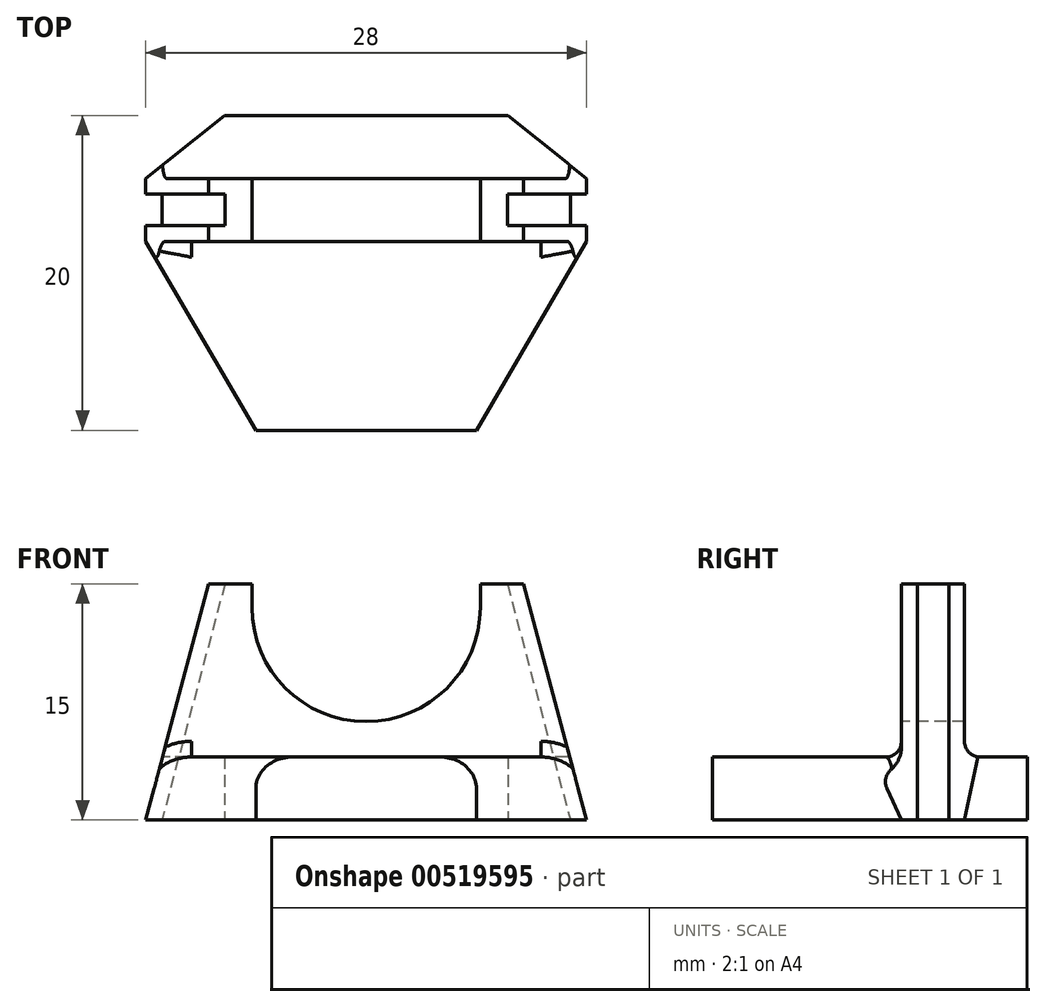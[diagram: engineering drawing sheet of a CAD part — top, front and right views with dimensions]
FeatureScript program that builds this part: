
annotation { "Feature Type Name" : "Feature", "Feature Type Description" : "" }
export const myFeature = defineFeature(function(context is Context, id is Id, definition is map)
    precondition{}
    {
        {
            var Q0;
            Q0=qCreatedBy(makeId("Top.planeOp"),FACE);
            var sketch = newSketch(context, id + "F0", { "sketchPlane" : qUnion([Q0])});
            skLineSegment(sketch, "E0.bottom", {"start": v(-14, 10) * mm, "end": v(14, 10) * mm});
            skLineSegment(sketch, "E0.top", {"start": v(-14, -10) * mm, "end": v(14, -10) * mm});
            skLineSegment(sketch, "E0.left", {"start": v(-14, 10) * mm, "end": v(-14, -10) * mm});
            skLineSegment(sketch, "E0.right", {"start": v(14, 10) * mm, "end": v(14, -10) * mm});
            skSolve(sketch);
        }
        {
            var Q0;
            Q0 = qSketchRegion(id + "F0", true);
            extrude(context, id + "F1", {"entities" : qUnion([Q0]), "depth" : 15 * mm, "offsetDistance" : 25 * mm});
        }
        {
            var Q0;
            Q0=qCreatedBy(makeId("Right.planeOp"),FACE);
            var sketch = newSketch(context, id + "F2", { "sketchPlane" : qUnion([Q0])});
            skLineSegment(sketch, "E1.bottom", {"start": v(-10, 15) * mm, "end": v(2, 15) * mm});
            skLineSegment(sketch, "E1.top", {"start": v(-10, 4) * mm, "end": v(2, 4) * mm});
            skLineSegment(sketch, "E1.left", {"start": v(-10, 15) * mm, "end": v(-10, 4) * mm});
            skLineSegment(sketch, "E1.right", {"start": v(2, 15) * mm, "end": v(2, 4) * mm});
            skSolve(sketch);
        }
        {
            var Q0;
            Q0 = qSketchRegion(id + "F2", true);
            extrude(context, id + "F3", {"entities" : qUnion([Q0]), "endBound" : BoundingType.SYMMETRIC, "depth" : 28 * mm, "offsetDistance" : 25 * mm});
        }
        {
            var Q0;
            Q0=qCreatedBy(makeId("Front.planeOp"),FACE);
            var sketch = newSketch(context, id + "F4", { "sketchPlane" : qUnion([Q0])});
            skCircle(sketch, "E2", {"center": v(0, 13.5) * mm, "radius": 7.25 * mm});
            skLineSegment(sketch, "E3.bottom", {"start": v(-7.25, 13.5) * mm, "end": v(7.25, 13.5) * mm});
            skLineSegment(sketch, "E3.top", {"start": v(-7.25, 22.5) * mm, "end": v(7.25, 22.5) * mm});
            skLineSegment(sketch, "E3.left", {"start": v(-7.25, 13.5) * mm, "end": v(-7.25, 22.5) * mm});
            skLineSegment(sketch, "E3.right", {"start": v(7.25, 13.5) * mm, "end": v(7.25, 22.5) * mm});
            skSolve(sketch);
        }
        {
            var Q0;
            Q0 = qSketchRegion(id + "F4", true);
            extrude(context, id + "F5", {"entities" : qUnion([Q0]), "oppositeDirection" : true, "depth" : 25 * mm, "offsetDistance" : 25 * mm});
        }
        {
            var Q0;
            Q0=qCreatedBy(makeId("Front.planeOp"),FACE);
            var sketch = newSketch(context, id + "F6", { "sketchPlane" : qUnion([Q0])});
            skLineSegment(sketch, "E4", {"start": v(-14, 15) * mm, "end": v(-10, 15) * mm});
            skLineSegment(sketch, "E5", {"start": v(-10, 15) * mm, "end": v(-14, 0) * mm});
            skLineSegment(sketch, "E6", {"start": v(-14, 0) * mm, "end": v(-14, 15) * mm});
            skSolve(sketch);
        }
        {
            var Q0;
            Q0 = qSketchRegion(id + "F6", true);
            extrude(context, id + "F7", {"entities" : qUnion([Q0]), "endBound" : BoundingType.SYMMETRIC, "depth" : 20 * mm, "offsetDistance" : 25 * mm});
        }
        {
            var Q0;
            Q0=makeQuery(id+"F7.opExtrude","SWEPT_BODY",BODY,{"disambiguationData":[OSD([sQuery(id+"F6.wireOp",EDGE,"E4"),sQuery(id+"F6.wireOp",EDGE,"E5"),sQuery(id+"F6.wireOp",EDGE,"E6")])]});
            var Q1;
            Q1=qCreatedBy(makeId("Right.planeOp"),FACE);
            mirror(context, id + "F8", {"entities" : qUnion([Q0]), "mirrorPlane" : qUnion([Q1])});
        }
        {
            var Q0;
            Q0=qCreatedBy(makeId("Right.planeOp"),FACE);
            var sketch = newSketch(context, id + "F9", { "sketchPlane" : qUnion([Q0])});
            skLineSegment(sketch, "E7.bottom", {"start": v(6, 15) * mm, "end": v(10, 15) * mm});
            skLineSegment(sketch, "E7.top", {"start": v(6, 4) * mm, "end": v(10, 4) * mm});
            skLineSegment(sketch, "E7.left", {"start": v(6, 15) * mm, "end": v(6, 4) * mm});
            skLineSegment(sketch, "E7.right", {"start": v(10, 15) * mm, "end": v(10, 4) * mm});
            skSolve(sketch);
        }
        {
            var Q0;
            Q0 = qSketchRegion(id + "F9", true);
            extrude(context, id + "F10", {"entities" : qUnion([Q0]), "endBound" : BoundingType.SYMMETRIC, "depth" : 28 * mm, "offsetDistance" : 25 * mm});
        }
        {
            var Q0;
            Q0=qCreatedBy(makeId("Top.planeOp"),FACE);
            var sketch = newSketch(context, id + "F11", { "sketchPlane" : qUnion([Q0])});
            skLineSegment(sketch, "E8", {"start": v(-9, 10) * mm, "end": v(-14, 10) * mm});
            skLineSegment(sketch, "E9", {"start": v(-14, 10) * mm, "end": v(-14, 6) * mm});
            skLineSegment(sketch, "E10", {"start": v(-14, 6) * mm, "end": v(-9, 10) * mm});
            skSolve(sketch);
        }
        {
            var Q0;
            Q0 = qSketchRegion(id + "F11", true);
            extrude(context, id + "F12", {"entities" : qUnion([Q0]), "depth" : 15 * mm, "offsetDistance" : 25 * mm});
        }
        {
            var Q0;
            Q0=makeQuery(id+"F12.opExtrude","SWEPT_BODY",BODY,{"disambiguationData":[OSD([sQuery(id+"F11.wireOp",EDGE,"E8"),sQuery(id+"F11.wireOp",EDGE,"E9"),sQuery(id+"F11.wireOp",EDGE,"E10")])]});
            var Q1;
            Q1=qCreatedBy(makeId("Right.planeOp"),FACE);
            mirror(context, id + "F13", {"entities" : qUnion([Q0]), "mirrorPlane" : qUnion([Q1])});
        }
        {
            var Q0;
            Q0=qCreatedBy(makeId("Top.planeOp"),FACE);
            var sketch = newSketch(context, id + "F14", { "sketchPlane" : qUnion([Q0])});
            skLineSegment(sketch, "E11", {"start": v(-7, -10) * mm, "end": v(-14, -10) * mm});
            skLineSegment(sketch, "E12", {"start": v(-14, -10) * mm, "end": v(-14, 2) * mm});
            skLineSegment(sketch, "E13", {"start": v(-14, 2) * mm, "end": v(-7, -10) * mm});
            skSolve(sketch);
        }
        {
            var Q0;
            Q0 = qSketchRegion(id + "F14", true);
            extrude(context, id + "F15", {"entities" : qUnion([Q0]), "depth" : 15 * mm, "offsetDistance" : 25 * mm});
        }
        {
            var Q0;
            Q0=makeQuery(id+"F15.opExtrude","SWEPT_BODY",BODY,{"disambiguationData":[OSD([sQuery(id+"F14.wireOp",EDGE,"E11"),sQuery(id+"F14.wireOp",EDGE,"E12"),sQuery(id+"F14.wireOp",EDGE,"E13")])]});
            var Q1;
            Q1=qCreatedBy(makeId("Right.planeOp"),FACE);
            mirror(context, id + "F16", {"entities" : qUnion([Q0]), "mirrorPlane" : qUnion([Q1])});
        }
        {
            var Q0;
            Q0=makeQuery(id+"F3.opExtrude","SWEPT_BODY",BODY,{"disambiguationData":[OSD([sQuery(id+"F2.wireOp",EDGE,"E1.bottom"),sQuery(id+"F2.wireOp",EDGE,"E1.top"),sQuery(id+"F2.wireOp",EDGE,"E1.left"),sQuery(id+"F2.wireOp",EDGE,"E1.right")])]});
            var Q1;
            Q1=makeQuery(id+"F5.opExtrude","SWEPT_BODY",BODY,{"disambiguationData":[OSD([sQuery(id+"F4.wireOp",EDGE,"E2"),sQuery(id+"F4.wireOp",EDGE,"E3.top"),sQuery(id+"F4.wireOp",EDGE,"E3.left"),sQuery(id+"F4.wireOp",EDGE,"E3.right")])]});
            var Q2;
            Q2=makeQuery(id+"F7.opExtrude","SWEPT_BODY",BODY,{"disambiguationData":[OSD([sQuery(id+"F6.wireOp",EDGE,"E4"),sQuery(id+"F6.wireOp",EDGE,"E5"),sQuery(id+"F6.wireOp",EDGE,"E6")])]});
            var Q3;
            Q3=makeQuery(id+"F8.opPattern","COPY",BODY,{"derivedFrom":makeQuery(id+"F7.opExtrude","SWEPT_BODY",BODY,{"disambiguationData":[OSD([sQuery(id+"F6.wireOp",EDGE,"E4"),sQuery(id+"F6.wireOp",EDGE,"E5"),sQuery(id+"F6.wireOp",EDGE,"E6")])]}),"instanceName":"1"});
            var Q4;
            Q4=makeQuery(id+"F10.opExtrude","SWEPT_BODY",BODY,{"disambiguationData":[OSD([sQuery(id+"F9.wireOp",EDGE,"E7.bottom"),sQuery(id+"F9.wireOp",EDGE,"E7.top"),sQuery(id+"F9.wireOp",EDGE,"E7.left"),sQuery(id+"F9.wireOp",EDGE,"E7.right")])]});
            var Q5;
            Q5=makeQuery(id+"FawOFgsiVvA8u39_4.opExtrude","SWEPT_BODY",BODY,{"disambiguationData":[OSD([sQuery(id+"FQr5FlxrUfjwjdP_4.wireOp",EDGE,"HyzrT1vO-Ye7J-sqqj-sUMt-KC3yQP7SDtpv.bottom"),sQuery(id+"FQr5FlxrUfjwjdP_4.wireOp",EDGE,"HyzrT1vO-Ye7J-sqqj-sUMt-KC3yQP7SDtpv.top"),sQuery(id+"FQr5FlxrUfjwjdP_4.wireOp",EDGE,"HyzrT1vO-Ye7J-sqqj-sUMt-KC3yQP7SDtpv.left"),sQuery(id+"FQr5FlxrUfjwjdP_4.wireOp",EDGE,"HyzrT1vO-Ye7J-sqqj-sUMt-KC3yQP7SDtpv.right")])]});
            var Q6;
            Q6=makeQuery(id+"FKkhov8mjdonEyy_5.opPattern","COPY",BODY,{"derivedFrom":makeQuery(id+"FawOFgsiVvA8u39_4.opExtrude","SWEPT_BODY",BODY,{"disambiguationData":[OSD([sQuery(id+"FQr5FlxrUfjwjdP_4.wireOp",EDGE,"HyzrT1vO-Ye7J-sqqj-sUMt-KC3yQP7SDtpv.bottom"),sQuery(id+"FQr5FlxrUfjwjdP_4.wireOp",EDGE,"HyzrT1vO-Ye7J-sqqj-sUMt-KC3yQP7SDtpv.top"),sQuery(id+"FQr5FlxrUfjwjdP_4.wireOp",EDGE,"HyzrT1vO-Ye7J-sqqj-sUMt-KC3yQP7SDtpv.left"),sQuery(id+"FQr5FlxrUfjwjdP_4.wireOp",EDGE,"HyzrT1vO-Ye7J-sqqj-sUMt-KC3yQP7SDtpv.right")])]}),"instanceName":"1"});
            var Q7;
            Q7=makeQuery(id+"F12.opExtrude","SWEPT_BODY",BODY,{"disambiguationData":[OSD([sQuery(id+"F11.wireOp",EDGE,"E8"),sQuery(id+"F11.wireOp",EDGE,"E9"),sQuery(id+"F11.wireOp",EDGE,"E10")])]});
            var Q8;
            Q8=makeQuery(id+"F13.opPattern","COPY",BODY,{"derivedFrom":makeQuery(id+"F12.opExtrude","SWEPT_BODY",BODY,{"disambiguationData":[OSD([sQuery(id+"F11.wireOp",EDGE,"E8"),sQuery(id+"F11.wireOp",EDGE,"E9"),sQuery(id+"F11.wireOp",EDGE,"E10")])]}),"instanceName":"1"});
            var Q9;
            Q9=makeQuery(id+"F15.opExtrude","SWEPT_BODY",BODY,{"disambiguationData":[OSD([sQuery(id+"F14.wireOp",EDGE,"E11"),sQuery(id+"F14.wireOp",EDGE,"E12"),sQuery(id+"F14.wireOp",EDGE,"E13")])]});
            var Q10;
            Q10=makeQuery(id+"F16.opPattern","COPY",BODY,{"derivedFrom":makeQuery(id+"F15.opExtrude","SWEPT_BODY",BODY,{"disambiguationData":[OSD([sQuery(id+"F14.wireOp",EDGE,"E11"),sQuery(id+"F14.wireOp",EDGE,"E12"),sQuery(id+"F14.wireOp",EDGE,"E13")])]}),"instanceName":"1"});
            var Q11;
            Q11=makeQuery(id+"F1.opExtrude","SWEPT_BODY",BODY,{"disambiguationData":[OSD([sQuery(id+"F0.wireOp",EDGE,"E0.bottom"),sQuery(id+"F0.wireOp",EDGE,"E0.top"),sQuery(id+"F0.wireOp",EDGE,"E0.left"),sQuery(id+"F0.wireOp",EDGE,"E0.right")])]});
            booleanBodies(context, id + "F17", {"operationType" : BooleanOperationType.SUBTRACTION, "tools" : qUnion([Q0, Q1, Q2, Q3, Q4, Q5, Q6, Q7, Q8, Q9, Q10]), "targets" : qUnion([Q11])});
        }
        {
            var Q0;
            Q0=makeQuery(id+"F17.opBoolean","COPY",FACE,{"derivedFrom":makeQuery(id+"F7.opExtrude","SWEPT_FACE",FACE,{"disambiguationData":[OSD([sQuery(id+"F6.wireOp",EDGE,"E5")])]})});
            var sketch = newSketch(context, id + "F18", { "sketchPlane" : qUnion([Q0])});
            skLineSegment(sketch, "E14.bottom", {"start": v(-5, 13.92) * mm, "end": v(-3, 13.92) * mm});
            skLineSegment(sketch, "E14.top", {"start": v(-5, -3.6) * mm, "end": v(-3, -3.6) * mm});
            skLineSegment(sketch, "E14.left", {"start": v(-5, 13.92) * mm, "end": v(-5, -3.6) * mm});
            skLineSegment(sketch, "E14.right", {"start": v(-3, 13.92) * mm, "end": v(-3, -3.6) * mm});
            skSolve(sketch);
        }
        {
            var Q0;
            Q0 = qSketchRegion(id + "F18", true);
            extrude(context, id + "F19", {"entities" : qUnion([Q0]), "oppositeDirection" : true, "depth" : 1 * mm, "offsetDistance" : 25 * mm});
        }
        {
            var Q0;
            Q0=makeQuery(id+"F19.opExtrude","SWEPT_BODY",BODY,{"disambiguationData":[OSD([sQuery(id+"F18.wireOp",EDGE,"E14.bottom"),sQuery(id+"F18.wireOp",EDGE,"E14.top"),sQuery(id+"F18.wireOp",EDGE,"E14.left"),sQuery(id+"F18.wireOp",EDGE,"E14.right")])]});
            var Q1;
            Q1=qCreatedBy(makeId("Right.planeOp"),FACE);
            mirror(context, id + "F20", {"entities" : qUnion([Q0]), "mirrorPlane" : qUnion([Q1])});
        }
        {
            var Q0;
            Q0=makeQuery(id+"F20.opPattern","COPY",BODY,{"derivedFrom":makeQuery(id+"F19.opExtrude","SWEPT_BODY",BODY,{"disambiguationData":[OSD([sQuery(id+"F18.wireOp",EDGE,"E14.bottom"),sQuery(id+"F18.wireOp",EDGE,"E14.top"),sQuery(id+"F18.wireOp",EDGE,"E14.left"),sQuery(id+"F18.wireOp",EDGE,"E14.right")])]}),"instanceName":"1"});
            var Q1;
            Q1=makeQuery(id+"F19.opExtrude","SWEPT_BODY",BODY,{"disambiguationData":[OSD([sQuery(id+"F18.wireOp",EDGE,"E14.bottom"),sQuery(id+"F18.wireOp",EDGE,"E14.top"),sQuery(id+"F18.wireOp",EDGE,"E14.left"),sQuery(id+"F18.wireOp",EDGE,"E14.right")])]});
            var Q2;
            Q2=makeQuery(id+"F1.opExtrude","SWEPT_BODY",BODY,{"disambiguationData":[OSD([sQuery(id+"F0.wireOp",EDGE,"E0.bottom"),sQuery(id+"F0.wireOp",EDGE,"E0.top"),sQuery(id+"F0.wireOp",EDGE,"E0.left"),sQuery(id+"F0.wireOp",EDGE,"E0.right")])]});
            booleanBodies(context, id + "F21", {"operationType" : BooleanOperationType.SUBTRACTION, "tools" : qUnion([Q0, Q1]), "targets" : qUnion([Q2])});
        }
        {
            var Q0;
            Q0=makeQuery(id+"F17.opBoolean","COPY",EDGE,{"derivedFrom":makeQuery(id+"F13.opPattern","COPY",EDGE,{"derivedFrom":makeQuery(id+"F12.opExtrude","SWEPT_EDGE",EDGE,{"disambiguationData":[OSD([sQuery(id+"F11.wireOp",EDGE,"E8"),sQuery(id+"F11.wireOp",EDGE,"E10")])]}),"instanceName":"1"})});
            var Q1;
            Q1=makeQuery(id+"F17.opBoolean","COPY",EDGE,{"derivedFrom":makeQuery(id+"F12.opExtrude","SWEPT_EDGE",EDGE,{"disambiguationData":[OSD([sQuery(id+"F11.wireOp",EDGE,"E8"),sQuery(id+"F11.wireOp",EDGE,"E10")])]})});
            var Q2;
            Q2=makeQuery(id+"F17.opBoolean","COPY",EDGE,{"derivedFrom":makeQuery(id+"F10.opExtrude","SWEPT_EDGE",EDGE,{"disambiguationData":[OSD([sQuery(id+"F9.wireOp",EDGE,"E7.top"),sQuery(id+"F9.wireOp",EDGE,"E7.right")])]})});
            var Q3;
            Q3=makeQuery(id+"F17.opBoolean","INTERSECT",EDGE,{"derivedFrom":[makeQuery(id+"F3.opExtrude","SWEPT_FACE",FACE,{"disambiguationData":[OSD([sQuery(id+"F2.wireOp",EDGE,"E1.top")])]}),makeQuery(id+"F15.opExtrude","SWEPT_FACE",FACE,{"disambiguationData":[OSD([sQuery(id+"F14.wireOp",EDGE,"E13")])]})]});
            var Q4;
            Q4=makeQuery(id+"F17.opBoolean","COPY",EDGE,{"derivedFrom":makeQuery(id+"F3.opExtrude","SWEPT_EDGE",EDGE,{"disambiguationData":[OSD([sQuery(id+"F2.wireOp",EDGE,"E1.top"),sQuery(id+"F2.wireOp",EDGE,"E1.left")])]})});
            var Q5;
            Q5=makeQuery(id+"F17.opBoolean","INTERSECT",EDGE,{"derivedFrom":[makeQuery(id+"F3.opExtrude","SWEPT_FACE",FACE,{"disambiguationData":[OSD([sQuery(id+"F2.wireOp",EDGE,"E1.top")])]}),makeQuery(id+"F16.opPattern","COPY",FACE,{"derivedFrom":makeQuery(id+"F15.opExtrude","SWEPT_FACE",FACE,{"disambiguationData":[OSD([sQuery(id+"F14.wireOp",EDGE,"E13")])]}),"instanceName":"1"})]});
            fillet(context, id + "F22", {"entities" : qUnion([Q0, Q1, Q2, Q3, Q4, Q5]), "radius" : 2 * mm, "tangentPropagation" : true, "allowEdgeOverflow" : false});
        }
        {
            var Q0;
            Q0=makeQuery(id+"F17.opBoolean","COPY",EDGE,{"derivedFrom":makeQuery(id+"F3.opExtrude","SWEPT_EDGE",EDGE,{"disambiguationData":[OSD([sQuery(id+"F2.wireOp",EDGE,"E1.top"),sQuery(id+"F2.wireOp",EDGE,"E1.right")])]})});
            var Q1;
            Q1=makeQuery(id+"F17.opBoolean","COPY",EDGE,{"derivedFrom":makeQuery(id+"F10.opExtrude","SWEPT_EDGE",EDGE,{"disambiguationData":[OSD([sQuery(id+"F9.wireOp",EDGE,"E7.top"),sQuery(id+"F9.wireOp",EDGE,"E7.left")])]})});
            fillet(context, id + "F23", {"entities" : qUnion([Q0, Q1]), "radius" : 1 * mm, "tangentPropagation" : true, "allowEdgeOverflow" : false});
        }
    });
